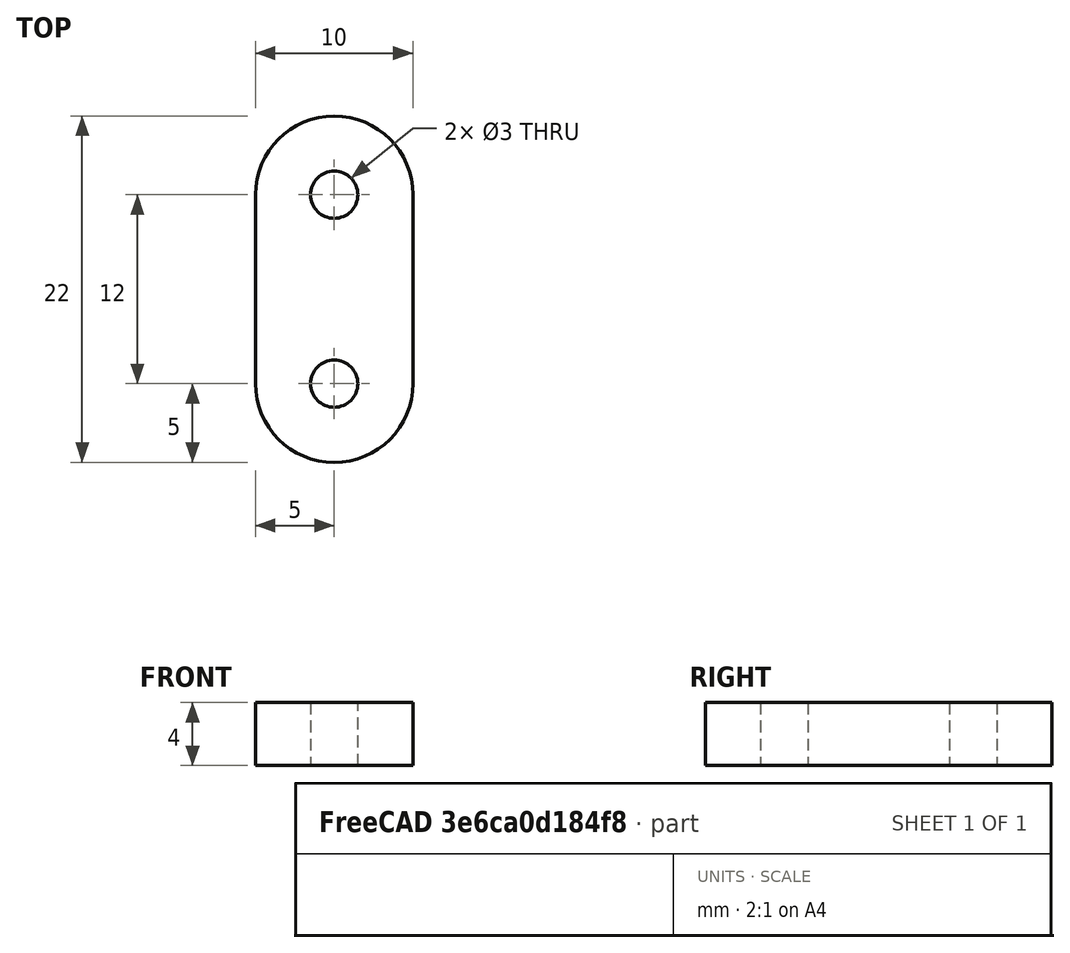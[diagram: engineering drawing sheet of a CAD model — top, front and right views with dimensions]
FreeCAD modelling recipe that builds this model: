
FCSTD DOCUMENT  (FreeCAD 0.16R6707 (Git))
Label: BeltClip
License: All rights reserved
LicenseURL: http://en.wikipedia.org/wiki/All_rights_reserved
objects: Sketcher::SketchObject×1, PartDesign::Pad×1
note: 3 computed .brp shape members not serialized (recipe doc carries the construction recipe); baked Part::Feature solids carry a one-line shape summary decoded from their .brp

FEATURE [Sketcher::SketchObject] Sketch
  sketch-geometry (6):
    g0: ArcOfCircle CenterX=0 CenterY=12 CenterZ=0 NormalX=0 NormalY=0 NormalZ=1 Radius=5 StartAngle=0 EndAngle=3.14159
    g1: ArcOfCircle CenterX=0 CenterY=0 CenterZ=0 NormalX=0 NormalY=0 NormalZ=1 Radius=5 StartAngle=3.14159 EndAngle=6.28319
    g2: LineSegment StartX=-5 StartY=12 StartZ=0 EndX=-5 EndY=1e-12 EndZ=0
    g3: LineSegment StartX=5 StartY=12 StartZ=0 EndX=5 EndY=0 EndZ=0
    g4: Circle CenterX=0 CenterY=12 CenterZ=0 NormalX=0 NormalY=0 NormalZ=1 Radius=1.5
    g5: Circle CenterX=0 CenterY=0 CenterZ=0 NormalX=0 NormalY=0 NormalZ=1 Radius=1.5
  constraints (13):
    c: Tangent(g0,g3) = 1.5708
    c: Tangent(g0,g2) = -1.5708
    c: Tangent(g2,g1) = -1.5708
    c: Tangent(g3,g1) = 1.5708
    c: Vertical(g2)
    c: Equal(g0,g1)
    c: Coincident(g5,g1)
    c: Coincident(g4,g0)
    c: Radius(g4) = 1.5
    c: Equal(g4,g5)
    c: Radius(g1) = 5
    c: DistanceY(g1,g0) = 12
    c: Coincident(g1,g-1)
FEATURE [PartDesign::Pad] Pad
  Length = 4
  Length2 = 100
  Sketch = -> Sketch
  Type = 0
